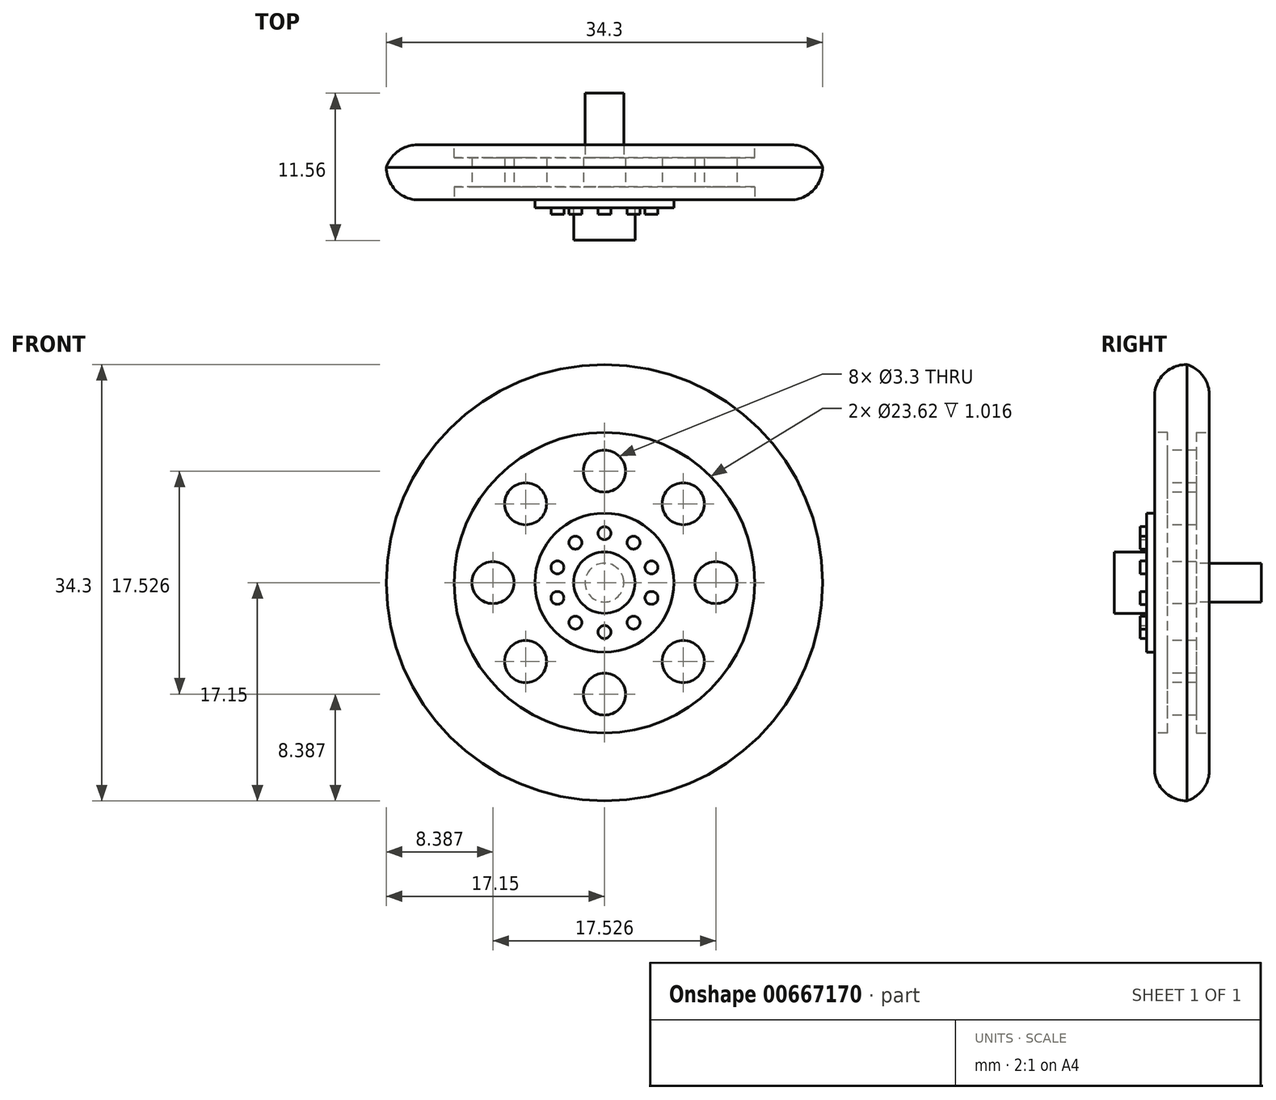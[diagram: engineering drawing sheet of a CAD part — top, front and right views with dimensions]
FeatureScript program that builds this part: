
annotation { "Feature Type Name" : "Feature", "Feature Type Description" : "" }
export const myFeature = defineFeature(function(context is Context, id is Id, definition is map)
    precondition{}
    {
        {
            var Q0;
            Q0=qCreatedBy(makeId("Front.planeOp"),FACE);
            var sketch = newSketch(context, id + "F0", { "sketchPlane" : qUnion([Q0])});
            skCircle(sketch, "E0", {"center": v(0, 0) * mm, "radius": 17.15 * mm});
            skSolve(sketch);
        }
        {
            var Q0;
            Q0=makeQuery(id+"F0.imprint","IMPRINT",FACE,{"disambiguationData":[TD([[makeQuery(id+"F0.imprint","IMPRINT",EDGE,{"derivedFrom":sQuery(id+"F0.wireOp",EDGE,"E0")}),1.0]])]});
            extrude(context, id + "F1", {"entities" : qUnion([Q0]), "oppositeDirection" : true, "depth" : 4.32 * mm, "offsetDistance" : 25.4 * mm});
        }
        {
            var Q0;
            Q0=makeQuery(id+"F1.opExtrude","CAP_EDGE",EDGE,{"disambiguationData":[OSD([sQuery(id+"F0.wireOp",EDGE,"E0")])],"isStart":true});
            fillet(context, id + "F2", {"entities" : qUnion([Q0]), "radius" : 2.54 * mm, "tangentPropagation" : true, "allowEdgeOverflow" : false});
        }
        {
            var Q0;
            Q0=makeQuery(id+"F1.opExtrude","CAP_EDGE",EDGE,{"disambiguationData":[OSD([sQuery(id+"F0.wireOp",EDGE,"E0")])],"isStart":false});
            fillet(context, id + "F3", {"entities" : qUnion([Q0]), "radius" : 2.54 * mm, "tangentPropagation" : true, "allowEdgeOverflow" : false});
        }
        {
            var Q0;
            Q0=makeQuery(id+"F1.opExtrude","CAP_FACE",FACE,{"disambiguationData":[OSD([sQuery(id+"F0.wireOp",EDGE,"E0")])],"isStart":true});
            var sketch = newSketch(context, id + "F4", { "sketchPlane" : qUnion([Q0])});
            skCircle(sketch, "E1", {"center": v(0, 0) * mm, "radius": 5.46 * mm});
            skSolve(sketch);
        }
        {
            var Q0;
            Q0=makeQuery(id+"F4.imprint","IMPRINT",FACE,{"disambiguationData":[TD([[makeQuery(id+"F4.imprint","IMPRINT",EDGE,{"derivedFrom":sQuery(id+"F4.wireOp",EDGE,"E1")}),1.0]])]});
            extrude(context, id + "F5", {"entities" : qUnion([Q0]), "operationType" : NewBodyOperationType.ADD, "depth" : 0.64 * mm, "offsetDistance" : 25.4 * mm});
        }
        {
            var Q0;
            Q0=makeQuery(id+"F5.opExtrude","CAP_FACE",FACE,{"disambiguationData":[OSD([sQuery(id+"F4.wireOp",EDGE,"E1")])],"isStart":false});
            var sketch = newSketch(context, id + "F6", { "sketchPlane" : qUnion([Q0])});
            skCircle(sketch, "E2", {"center": v(0, 0) * mm, "radius": 2.41 * mm});
            skSolve(sketch);
        }
        {
            var Q0;
            Q0=makeQuery(id+"F6.imprint","IMPRINT",FACE,{"disambiguationData":[TD([[makeQuery(id+"F6.imprint","IMPRINT",EDGE,{"derivedFrom":sQuery(id+"F6.wireOp",EDGE,"E2")}),1.0]])]});
            extrude(context, id + "F7", {"entities" : qUnion([Q0]), "operationType" : NewBodyOperationType.ADD, "depth" : 2.54 * mm, "offsetDistance" : 25.4 * mm});
        }
        {
            var Q0;
            Q0=makeQuery(id+"F1.opExtrude","CAP_FACE",FACE,{"disambiguationData":[OSD([sQuery(id+"F0.wireOp",EDGE,"E0")])],"isStart":true});
            var sketch = newSketch(context, id + "F8", { "sketchPlane" : qUnion([Q0])});
            skCircle(sketch, "E3", {"center": v(0, 0) * mm, "radius": 11.81 * mm});
            skSolve(sketch);
        }
        {
            var Q0;
            Q0=makeQuery(id+"F8.imprint","IMPRINT",FACE,{"disambiguationData":[TD([[makeQuery(id+"F8.imprint","IMPRINT",EDGE,{"derivedFrom":sQuery(id+"F8.wireOp",EDGE,"E3")}),1.0]])]});
            var sketch = newSketch(context, id + "F9", { "sketchPlane" : qUnion([Q0])});
            skCircle(sketch, "E4", {"center": v(0, 8.76) * mm, "radius": 1.65 * mm});
            skCircle(sketch, "E5.1.0", {"center": v(-6.2, 6.2) * mm, "radius": 1.65 * mm});
            skCircle(sketch, "E5.2.0", {"center": v(-8.76, 0) * mm, "radius": 1.65 * mm});
            skCircle(sketch, "E5.3.0", {"center": v(-6.2, -6.2) * mm, "radius": 1.65 * mm});
            skCircle(sketch, "E5.4.0", {"center": v(0, -8.76) * mm, "radius": 1.65 * mm});
            skCircle(sketch, "E5.5.0", {"center": v(6.2, -6.2) * mm, "radius": 1.65 * mm});
            skCircle(sketch, "E5.6.0", {"center": v(8.76, 0) * mm, "radius": 1.65 * mm});
            skCircle(sketch, "E5.7.0", {"center": v(6.2, 6.2) * mm, "radius": 1.65 * mm});
            skPoint(sketch, "E5.center", {"position": v(0, 0) * mm});
            skSolve(sketch);
        }
        {
            var Q0;
            Q0=makeQuery(id+"F9.imprint","IMPRINT",FACE,{"disambiguationData":[TD([[makeQuery(id+"F9.imprint","IMPRINT",EDGE,{"derivedFrom":sQuery(id+"F9.wireOp",EDGE,"E5.4.0")}),1.0]])]});
            var Q1;
            Q1=makeQuery(id+"F9.imprint","IMPRINT",FACE,{"disambiguationData":[TD([[makeQuery(id+"F9.imprint","IMPRINT",EDGE,{"derivedFrom":sQuery(id+"F9.wireOp",EDGE,"E5.5.0")}),1.0]])]});
            var Q2;
            Q2=makeQuery(id+"F9.imprint","IMPRINT",FACE,{"disambiguationData":[TD([[makeQuery(id+"F9.imprint","IMPRINT",EDGE,{"derivedFrom":sQuery(id+"F9.wireOp",EDGE,"E5.6.0")}),1.0]])]});
            var Q3;
            Q3=makeQuery(id+"F9.imprint","IMPRINT",FACE,{"disambiguationData":[TD([[makeQuery(id+"F9.imprint","IMPRINT",EDGE,{"derivedFrom":sQuery(id+"F9.wireOp",EDGE,"E5.7.0")}),1.0]])]});
            var Q4;
            Q4=makeQuery(id+"F9.imprint","IMPRINT",FACE,{"disambiguationData":[TD([[makeQuery(id+"F9.imprint","IMPRINT",EDGE,{"derivedFrom":sQuery(id+"F9.wireOp",EDGE,"E5.2.0")}),1.0]])]});
            var Q5;
            Q5=makeQuery(id+"F9.imprint","IMPRINT",FACE,{"disambiguationData":[TD([[makeQuery(id+"F9.imprint","IMPRINT",EDGE,{"derivedFrom":sQuery(id+"F9.wireOp",EDGE,"E4")}),1.0]])]});
            var Q6;
            Q6=makeQuery(id+"F9.imprint","IMPRINT",FACE,{"disambiguationData":[TD([[makeQuery(id+"F9.imprint","IMPRINT",EDGE,{"derivedFrom":sQuery(id+"F9.wireOp",EDGE,"E5.1.0")}),1.0]])]});
            var Q7;
            Q7=makeQuery(id+"F9.imprint","IMPRINT",FACE,{"disambiguationData":[TD([[makeQuery(id+"F9.imprint","IMPRINT",EDGE,{"derivedFrom":sQuery(id+"F9.wireOp",EDGE,"E5.3.0")}),1.0]])]});
            extrude(context, id + "F10", {"entities" : qUnion([Q0, Q1, Q2, Q3, Q4, Q5, Q6, Q7]), "operationType" : NewBodyOperationType.REMOVE, "oppositeDirection" : true, "depth" : 25.4 * mm, "offsetDistance" : 25.4 * mm});
        }
        {
            var Q0;
            Q0=makeQuery(id+"F5.opExtrude","CAP_FACE",FACE,{"disambiguationData":[OSD([sQuery(id+"F4.wireOp",EDGE,"E1")])],"isStart":false});
            var sketch = newSketch(context, id + "F11", { "sketchPlane" : qUnion([Q0])});
            skCircle(sketch, "E6", {"center": v(0, 3.88) * mm, "radius": 0.5 * mm});
            skCircle(sketch, "E7.1.0", {"center": v(-2.28, 3.14) * mm, "radius": 0.5 * mm});
            skCircle(sketch, "E7.2.0", {"center": v(-3.7, 1.2) * mm, "radius": 0.5 * mm});
            skCircle(sketch, "E7.3.0", {"center": v(-3.7, -1.2) * mm, "radius": 0.5 * mm});
            skCircle(sketch, "E7.4.0", {"center": v(-2.28, -3.14) * mm, "radius": 0.5 * mm});
            skCircle(sketch, "E7.5.0", {"center": v(0, -3.88) * mm, "radius": 0.5 * mm});
            skCircle(sketch, "E7.6.0", {"center": v(2.28, -3.14) * mm, "radius": 0.5 * mm});
            skCircle(sketch, "E7.7.0", {"center": v(3.7, -1.2) * mm, "radius": 0.5 * mm});
            skCircle(sketch, "E7.8.0", {"center": v(3.7, 1.2) * mm, "radius": 0.5 * mm});
            skCircle(sketch, "E7.9.0", {"center": v(2.28, 3.14) * mm, "radius": 0.5 * mm});
            skPoint(sketch, "E7.center", {"position": v(0, 0) * mm});
            skSolve(sketch);
        }
        {
            var Q0;
            Q0=makeQuery(id+"F11.imprint","IMPRINT",FACE,{"disambiguationData":[TD([[makeQuery(id+"F11.imprint","IMPRINT",EDGE,{"derivedFrom":sQuery(id+"F11.wireOp",EDGE,"E6")}),1.0]])]});
            var Q1;
            Q1=makeQuery(id+"F11.imprint","IMPRINT",FACE,{"disambiguationData":[TD([[makeQuery(id+"F11.imprint","IMPRINT",EDGE,{"derivedFrom":sQuery(id+"F11.wireOp",EDGE,"E7.1.0")}),1.0]])]});
            var Q2;
            Q2=makeQuery(id+"F11.imprint","IMPRINT",FACE,{"disambiguationData":[TD([[makeQuery(id+"F11.imprint","IMPRINT",EDGE,{"derivedFrom":sQuery(id+"F11.wireOp",EDGE,"E7.2.0")}),1.0]])]});
            var Q3;
            Q3=makeQuery(id+"F11.imprint","IMPRINT",FACE,{"disambiguationData":[TD([[makeQuery(id+"F11.imprint","IMPRINT",EDGE,{"derivedFrom":sQuery(id+"F11.wireOp",EDGE,"E7.3.0")}),1.0]])]});
            var Q4;
            Q4=makeQuery(id+"F11.imprint","IMPRINT",FACE,{"disambiguationData":[TD([[makeQuery(id+"F11.imprint","IMPRINT",EDGE,{"derivedFrom":sQuery(id+"F11.wireOp",EDGE,"E7.4.0")}),1.0]])]});
            var Q5;
            Q5=makeQuery(id+"F11.imprint","IMPRINT",FACE,{"disambiguationData":[TD([[makeQuery(id+"F11.imprint","IMPRINT",EDGE,{"derivedFrom":sQuery(id+"F11.wireOp",EDGE,"E7.5.0")}),1.0]])]});
            var Q6;
            Q6=makeQuery(id+"F11.imprint","IMPRINT",FACE,{"disambiguationData":[TD([[makeQuery(id+"F11.imprint","IMPRINT",EDGE,{"derivedFrom":sQuery(id+"F11.wireOp",EDGE,"E7.9.0")}),1.0]])]});
            var Q7;
            Q7=makeQuery(id+"F11.imprint","IMPRINT",FACE,{"disambiguationData":[TD([[makeQuery(id+"F11.imprint","IMPRINT",EDGE,{"derivedFrom":sQuery(id+"F11.wireOp",EDGE,"E7.8.0")}),1.0]])]});
            var Q8;
            Q8=makeQuery(id+"F11.imprint","IMPRINT",FACE,{"disambiguationData":[TD([[makeQuery(id+"F11.imprint","IMPRINT",EDGE,{"derivedFrom":sQuery(id+"F11.wireOp",EDGE,"E7.7.0")}),1.0]])]});
            var Q9;
            Q9=makeQuery(id+"F11.imprint","IMPRINT",FACE,{"disambiguationData":[TD([[makeQuery(id+"F11.imprint","IMPRINT",EDGE,{"derivedFrom":sQuery(id+"F11.wireOp",EDGE,"E7.6.0")}),1.0]])]});
            extrude(context, id + "F12", {"entities" : qUnion([Q0, Q1, Q2, Q3, Q4, Q5, Q6, Q7, Q8, Q9]), "operationType" : NewBodyOperationType.ADD, "depth" : 0.5 * mm, "offsetDistance" : 25.4 * mm});
        }
        {
            var Q0;
            Q0 = qSketchRegion(id + "F8", true);
            extrude(context, id + "F13", {"entities" : qUnion([Q0]), "operationType" : NewBodyOperationType.REMOVE, "oppositeDirection" : true, "depth" : 1.02 * mm, "offsetDistance" : 25.4 * mm});
        }
        {
            var Q0;
            Q0=makeQuery(id+"F1.opExtrude","CAP_FACE",FACE,{"disambiguationData":[OSD([sQuery(id+"F0.wireOp",EDGE,"E0")])],"isStart":false});
            var sketch = newSketch(context, id + "F14", { "sketchPlane" : qUnion([Q0])});
            skCircle(sketch, "E8", {"center": v(0, 0) * mm, "radius": 11.81 * mm});
            skSolve(sketch);
        }
        {
            var Q0;
            Q0 = qSketchRegion(id + "F14", true);
            extrude(context, id + "F15", {"entities" : qUnion([Q0]), "operationType" : NewBodyOperationType.REMOVE, "oppositeDirection" : true, "depth" : 1.02 * mm, "offsetDistance" : 25.4 * mm});
        }
        {
            var Q0;
            Q0=makeQuery(id+"F15.boolean.opBoolean","COPY",FACE,{"derivedFrom":makeQuery(id+"F15.opExtrude","CAP_FACE",FACE,{"disambiguationData":[OSD([sQuery(id+"F14.wireOp",EDGE,"E8")])],"isStart":false})});
            var sketch = newSketch(context, id + "F16", { "sketchPlane" : qUnion([Q0])});
            skCircle(sketch, "E9", {"center": v(0, 0) * mm, "radius": 1.52 * mm});
            skSolve(sketch);
        }
        {
            var Q0;
            Q0=makeQuery(id+"F16.imprint","IMPRINT",FACE,{"disambiguationData":[TD([[makeQuery(id+"F16.imprint","IMPRINT",EDGE,{"derivedFrom":sQuery(id+"F16.wireOp",EDGE,"E9")}),1.0]])]});
            extrude(context, id + "F17", {"entities" : qUnion([Q0]), "operationType" : NewBodyOperationType.ADD, "depth" : 5.08 * mm, "offsetDistance" : 25.4 * mm});
        }
    });
